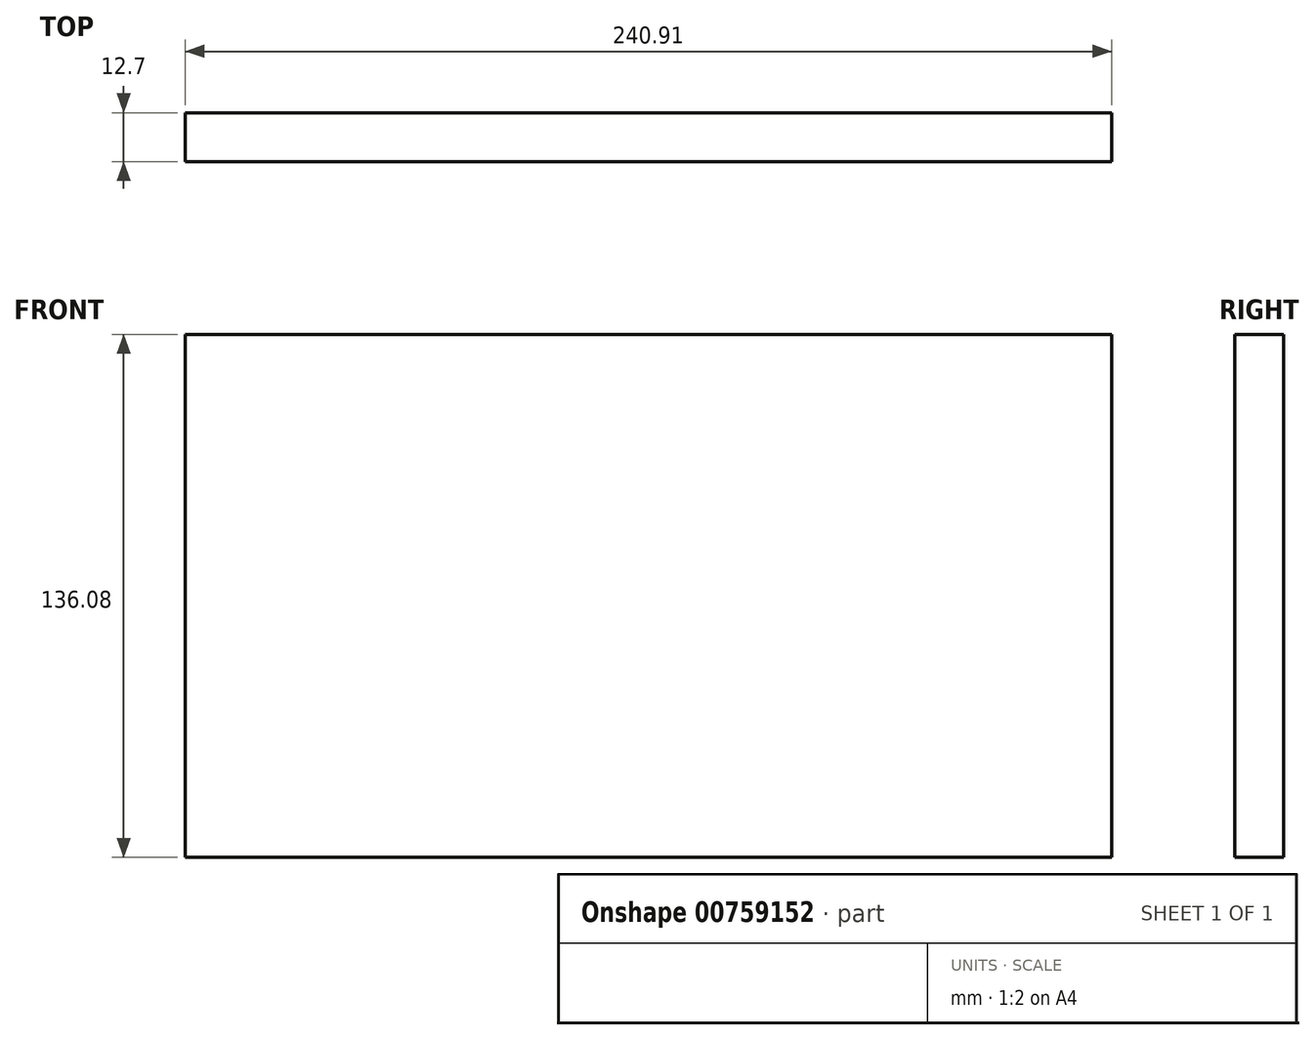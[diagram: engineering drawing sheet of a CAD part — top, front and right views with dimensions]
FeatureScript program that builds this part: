
annotation { "Feature Type Name" : "Feature", "Feature Type Description" : "" }
export const myFeature = defineFeature(function(context is Context, id is Id, definition is map)
    precondition{}
    {
        {
            var Q0;
            Q0=qCreatedBy(makeId("Front.planeOp"),FACE);
            var sketch = newSketch(context, id + "F0", { "sketchPlane" : qUnion([Q0])});
            skLineSegment(sketch, "E0.bottom", {"start": v(-114.03, 72.86) * mm, "end": v(126.88, 72.86) * mm});
            skLineSegment(sketch, "E0.top", {"start": v(-114.03, -63.22) * mm, "end": v(126.88, -63.22) * mm});
            skLineSegment(sketch, "E0.left", {"start": v(-114.03, 72.86) * mm, "end": v(-114.03, -63.22) * mm});
            skLineSegment(sketch, "E0.right", {"start": v(126.88, 72.86) * mm, "end": v(126.88, -63.22) * mm});
            skSolve(sketch);
        }
        {
            var Q0;
            Q0=makeQuery(id+"F0.imprint","IMPRINT",FACE,{"disambiguationData":[TD([[makeQuery(id+"F0.imprint","IMPRINT",EDGE,{"derivedFrom":sQuery(id+"F0.wireOp",EDGE,"E0.bottom")}),-1.0]])]});
            extrude(context, id + "F1", {"entities" : qUnion([Q0]), "endBound" : BoundingType.SYMMETRIC, "depth" : 12.7 * mm, "offsetDistance" : 25.4 * mm});
        }
    });
